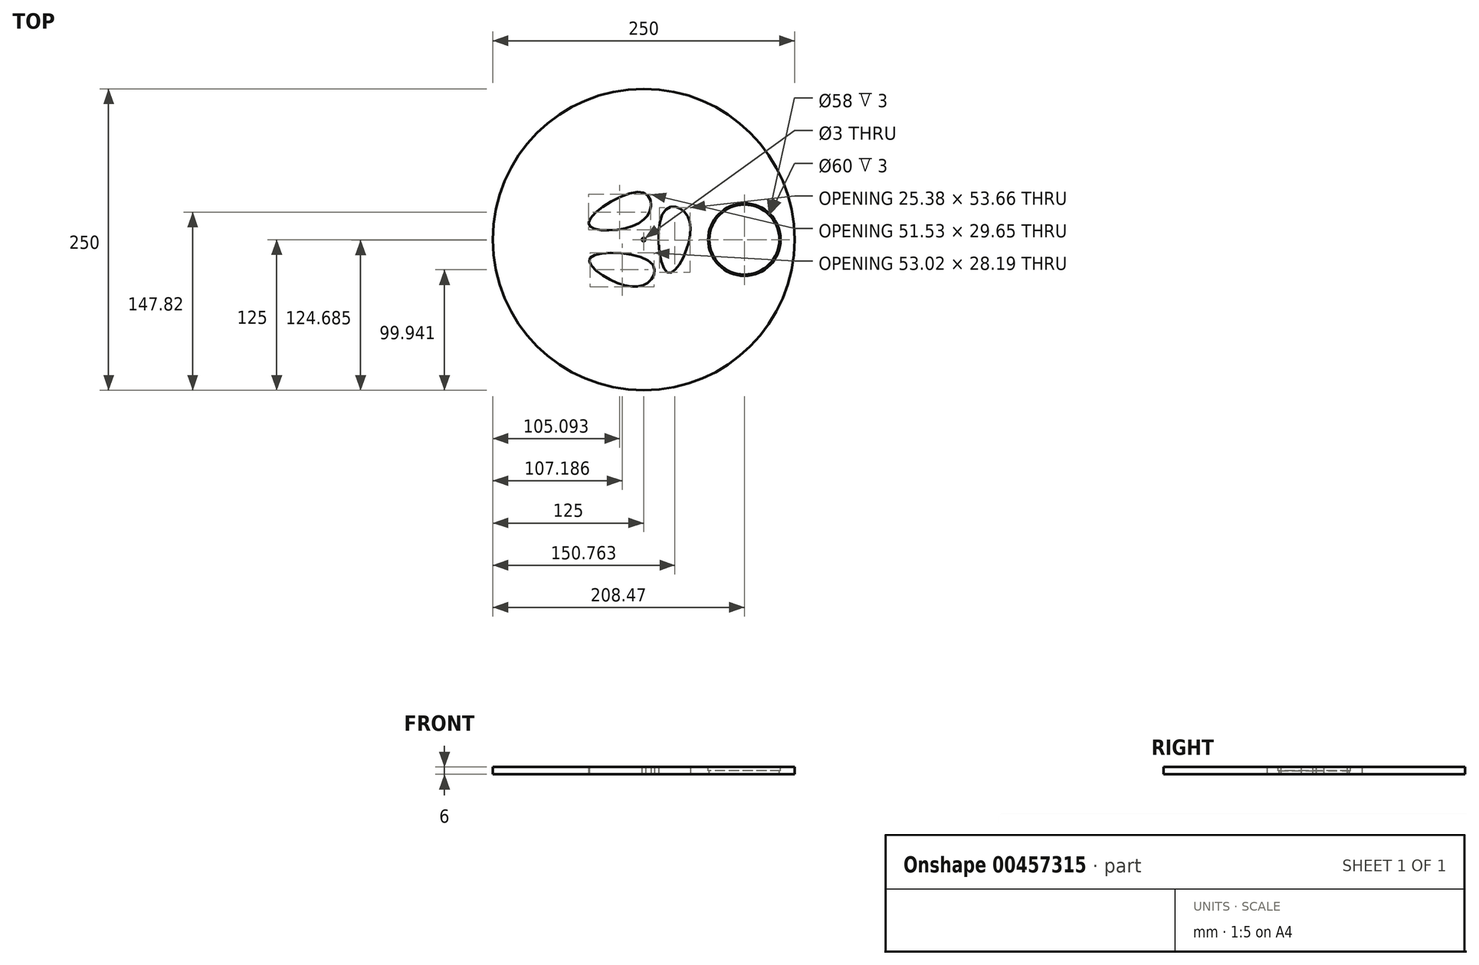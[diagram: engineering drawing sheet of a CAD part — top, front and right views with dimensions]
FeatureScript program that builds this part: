
annotation { "Feature Type Name" : "Feature", "Feature Type Description" : "" }
export const myFeature = defineFeature(function(context is Context, id is Id, definition is map)
    precondition{}
    {
        {
            var Q0;
            Q0=qCreatedBy(makeId("Top.planeOp"),FACE);
            var sketch = newSketch(context, id + "F0", { "sketchPlane" : qUnion([Q0])});
            skCircle(sketch, "E0", {"center": v(0, 0) * mm, "radius": 125 * mm});
            skSolve(sketch);
        }
        {
            var Q0;
            Q0 = qSketchRegion(id + "F0", true);
            extrude(context, id + "F1", {"entities" : qUnion([Q0]), "endBound" : BoundingType.SYMMETRIC, "depth" : 6 * mm});
        }
        {
            var Q0;
            Q0=makeQuery(id+"F1.opExtrude","CAP_FACE",FACE,{"disambiguationData":[OSD([sQuery(id+"F0.wireOp",EDGE,"E0")])],"isStart":true});
            var sketch = newSketch(context, id + "F2", { "sketchPlane" : qUnion([Q0])});
            skCircle(sketch, "E1", {"center": v(0, 0) * mm, "radius": 1.5 * mm});
            skSolve(sketch);
        }
        {
            var Q0;
            Q0 = qSketchRegion(id + "F2", true);
            extrude(context, id + "F3", {"entities" : qUnion([Q0]), "operationType" : NewBodyOperationType.REMOVE, "endBound" : BoundingType.THROUGH_ALL, "oppositeDirection" : true, "depth" : 25 * mm});
        }
        {
            var Q0;
            Q0=makeQuery(id+"F1.opExtrude","CAP_FACE",FACE,{"disambiguationData":[OSD([sQuery(id+"F0.wireOp",EDGE,"E0")])],"isStart":false});
            var sketch = newSketch(context, id + "F4", { "sketchPlane" : qUnion([Q0])});
            skCircle(sketch, "E2", {"center": v(0, 0) * mm, "radius": 83.5 * mm, "construction": true});
            skSolve(sketch);
        }
        {
            var Q0;
            {var subQ0=sQuery(id+"F0.wireOp",EDGE,"E0");Q0=makeQuery(id+"F4.imprint","IMPRINT",FACE,{"disambiguationData":[TD([[makeQuery(id+"F4.imprint","IMPRINT",EDGE,{"derivedFrom":makeQuery(id+"F1.opExtrude","CAP_EDGE",EDGE,{"disambiguationData":[OSD([subQ0])],"isStart":false})}),1.0]])]});}
            var sketch = newSketch(context, id + "F5", { "sketchPlane" : qUnion([Q0])});
            skCircle(sketch, "E3", {"center": v(83.47, 0) * mm, "radius": 30 * mm});
            skCircle(sketch, "E4", {"center": v(83.47, 0) * mm, "radius": 29 * mm});
            skSolve(sketch);
        }
        {
            var Q0;
            Q0=makeQuery(id+"F5.imprint","IMPRINT",FACE,{"disambiguationData":[TD([[makeQuery(id+"F5.imprint","IMPRINT",EDGE,{"derivedFrom":sQuery(id+"F5.wireOp",EDGE,"E4")}),1.0]])]});
            var Q1;
            Q1=sQuery(id+"F5.wireOp",EDGE,"E4");
            extrude(context, id + "F6", {"entities" : qUnion([Q0]), "operationType" : NewBodyOperationType.REMOVE, "surfaceEntities" : qUnion([Q1]), "endBound" : BoundingType.THROUGH_ALL, "oppositeDirection" : true, "depth" : 25 * mm});
        }
        {
            var Q0;
            Q0=makeQuery(id+"F5.imprint","IMPRINT",FACE,{"disambiguationData":[TD([[makeQuery(id+"F5.imprint","IMPRINT",EDGE,{"derivedFrom":sQuery(id+"F5.wireOp",EDGE,"E3")}),1.0]])]});
            extrude(context, id + "F7", {"entities" : qUnion([Q0]), "operationType" : NewBodyOperationType.REMOVE, "oppositeDirection" : true, "depth" : 3 * mm});
        }
        {
            var Q0;
            Q0=makeQuery(id+"F5.imprint","IMPRINT",FACE,{"disambiguationData":[TD([[makeQuery(id+"F5.imprint","IMPRINT",EDGE,{"derivedFrom":sQuery(id+"F5.wireOp",EDGE,"E3")}),-1.0]])]});
            var sketch = newSketch(context, id + "F8", { "sketchPlane" : qUnion([Q0])});
            skFitSpline(sketch, "E5", {"points": [v(-44.33, -15.05) * mm, v(-24.19, -35.11) * mm, v(3.98, -35.4) * mm, v(5.8, -18.88) * mm, v(-44.33, -15.05) * mm]});
            skFitSpline(sketch, "E6", {"points": [v(-45.67, 13.8) * mm, v(-17.67, 8.92) * mm, v(5.57, 24.83) * mm, v(-2.4, 39.42) * mm, v(-45.67, 13.8) * mm]});
            skFitSpline(sketch, "E7", {"points": [v(19.56, -27.14) * mm, v(36.74, -4.5) * mm, v(33.25, 23.46) * mm, v(16.62, 23.05) * mm, v(19.56, -27.14) * mm]});
            skSolve(sketch);
        }
        {
            var Q0;
            Q0 = qSketchRegion(id + "F8", true);
            extrude(context, id + "F9", {"entities" : qUnion([Q0]), "operationType" : NewBodyOperationType.REMOVE, "endBound" : BoundingType.THROUGH_ALL, "oppositeDirection" : true, "depth" : 25 * mm});
        }
    });
